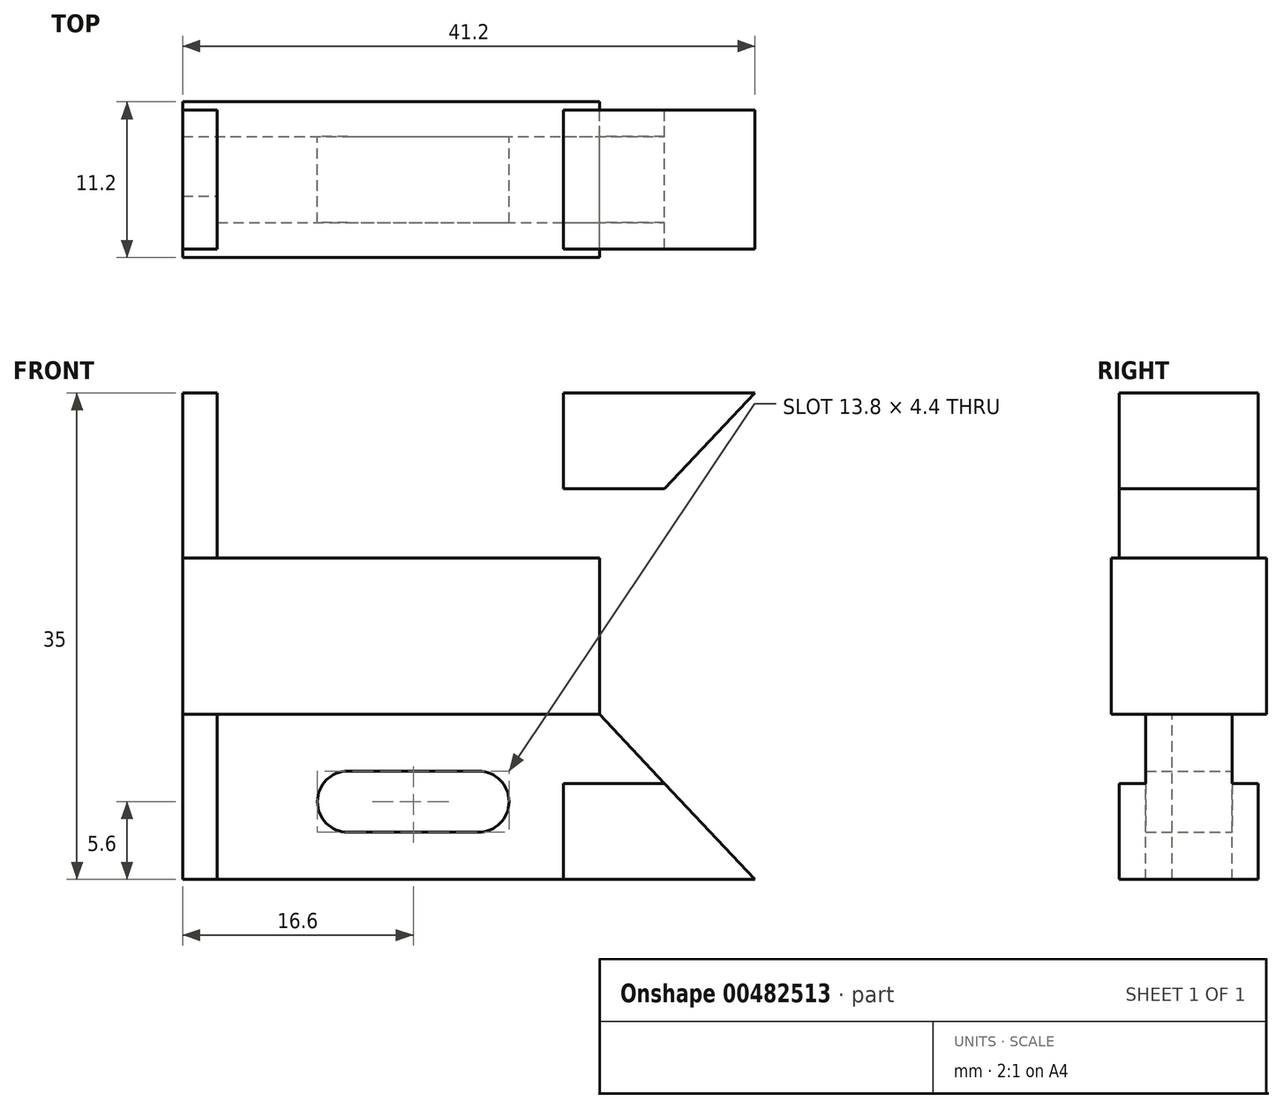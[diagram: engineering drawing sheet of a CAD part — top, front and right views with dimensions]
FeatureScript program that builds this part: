
annotation { "Feature Type Name" : "Feature", "Feature Type Description" : "" }
export const myFeature = defineFeature(function(context is Context, id is Id, definition is map)
    precondition{}
    {
        {
            var Q0;
            Q0=qCreatedBy(makeId("Front.planeOp"),FACE);
            var sketch = newSketch(context, id + "F0", { "sketchPlane" : qUnion([Q0])});
            skLineSegment(sketch, "E0.bottom", {"start": v(0, 0) * mm, "end": v(41.2, 0) * mm});
            skLineSegment(sketch, "E0.top", {"start": v(0, -11.88) * mm, "end": v(30, -11.88) * mm});
            skLineSegment(sketch, "E0.left", {"start": v(0, 0) * mm, "end": v(0, -11.88) * mm});
            skLineSegment(sketch, "E1.bottom", {"start": v(0, 0) * mm, "end": v(2.5, 0) * mm});
            skLineSegment(sketch, "E1.top", {"start": v(0, -11.88) * mm, "end": v(2.5, -11.88) * mm});
            skLineSegment(sketch, "E1.right", {"start": v(2.5, 0) * mm, "end": v(2.5, -11.88) * mm});
            skLineSegment(sketch, "E2.bottom", {"start": v(0, 0) * mm, "end": v(27.4, 0) * mm});
            skLineSegment(sketch, "E2.right", {"start": v(27.4, 0) * mm, "end": v(27.4, -6.9) * mm});
            skPoint(sketch, "E3.start.orphan", {"position": v(27.4, -6.9) * mm});
            skLineSegment(sketch, "E4", {"start": v(27.4, -6.9) * mm, "end": v(34.7, -6.9) * mm});
            skLineSegment(sketch, "E5", {"start": v(41.2, 0) * mm, "end": v(30, -11.88) * mm});
            skLineSegment(sketch, "E6.top", {"start": v(11.9, -3.4) * mm, "end": v(21.3, -3.4) * mm});
            skLineSegment(sketch, "E7.MirrorCS", {"start": v(11.9, -7.8) * mm, "end": v(21.3, -7.8) * mm});
            skLineSegment(sketch, "E8", {"start": v(23.5, -5.6) * mm, "end": v(23.5, -5.6) * mm});
            skLineSegment(sketch, "E9", {"start": v(9.7, -5.6) * mm, "end": v(9.7, -5.6) * mm});
            skPoint(sketch, "E10.visualSharp", {"position": v(9.7, -3.4) * mm});
            skArc(sketch, "E10.filletArc", {"start": v(11.9, -3.4) * mm, "mid": v(10.34, -4.04) * mm, "end": v(9.7, -5.6) * mm});
            skPoint(sketch, "E11.visualSharp", {"position": v(9.7, -7.8) * mm});
            skArc(sketch, "E11.filletArc", {"start": v(9.7, -5.6) * mm, "mid": v(10.34, -7.16) * mm, "end": v(11.9, -7.8) * mm});
            skPoint(sketch, "E12.visualSharp", {"position": v(23.5, -7.8) * mm});
            skArc(sketch, "E12.filletArc", {"start": v(21.3, -7.8) * mm, "mid": v(22.86, -7.16) * mm, "end": v(23.5, -5.6) * mm});
            skPoint(sketch, "E13.visualSharp", {"position": v(23.5, -3.4) * mm});
            skArc(sketch, "E13.filletArc", {"start": v(23.5, -5.6) * mm, "mid": v(22.86, -4.04) * mm, "end": v(21.3, -3.4) * mm});
            skLineSegment(sketch, "E14", {"start": v(0, -11.88) * mm, "end": v(0, -23.12) * mm});
            skLineSegment(sketch, "E15", {"start": v(0, -23.12) * mm, "end": v(30, -23.12) * mm});
            skLineSegment(sketch, "E16", {"start": v(30, -23.12) * mm, "end": v(30, -11.88) * mm});
            skLineSegment(sketch, "E17.MirrorCS", {"start": v(2.5, -35) * mm, "end": v(2.5, -23.13) * mm});
            skLineSegment(sketch, "E18.MirrorCS", {"start": v(0, -35) * mm, "end": v(0, -23.13) * mm});
            skLineSegment(sketch, "E19.MirrorCS", {"start": v(0, -35) * mm, "end": v(27.4, -35) * mm});
            skLineSegment(sketch, "E20.MirrorCS", {"start": v(0, -35) * mm, "end": v(41.2, -35) * mm});
            skLineSegment(sketch, "E21.MirrorCS", {"start": v(41.2, -35) * mm, "end": v(30, -23.12) * mm});
            skLineSegment(sketch, "E22.MirrorCS", {"start": v(27.4, -28.1) * mm, "end": v(34.7, -28.1) * mm});
            skLineSegment(sketch, "E23.MirrorCS", {"start": v(27.4, -35) * mm, "end": v(27.4, -28.1) * mm});
            skArc(sketch, "E24.MirrorCS", {"start": v(9.7, -29.4) * mm, "mid": v(10.34, -27.84) * mm, "end": v(11.9, -27.2) * mm});
            skArc(sketch, "E25.MirrorCS", {"start": v(11.9, -31.6) * mm, "mid": v(10.34, -30.96) * mm, "end": v(9.7, -29.4) * mm});
            skLineSegment(sketch, "E26.MirrorCS", {"start": v(11.9, -31.6) * mm, "end": v(21.3, -31.6) * mm});
            skLineSegment(sketch, "E27.MirrorCS", {"start": v(11.9, -27.2) * mm, "end": v(21.3, -27.2) * mm});
            skArc(sketch, "E28.MirrorCS", {"start": v(21.3, -27.2) * mm, "mid": v(22.86, -27.84) * mm, "end": v(23.5, -29.4) * mm});
            skArc(sketch, "E29.MirrorCS", {"start": v(23.5, -29.4) * mm, "mid": v(22.86, -30.96) * mm, "end": v(21.3, -31.6) * mm});
            skPoint(sketch, "E30.end.orphan", {"position": v(30, -17.5) * mm});
            skPoint(sketch, "E30.start.orphan", {"position": v(0, -17.5) * mm});
            skSolve(sketch);
        }
        {
            var Q0;
            Q0=makeQuery(id+"F0.imprint","IMPRINT",FACE,{"disambiguationData":[TD([[makeQuery(id+"F0.imprint","IMPRINT",EDGE,{"derivedFrom":sQuery(id+"F0.wireOp",EDGE,"E0.top")}),-1.0]])]});
            extrude(context, id + "F1", {"entities" : qUnion([Q0]), "depth" : 5.6 * mm, "hasSecondDirection" : true, "secondDirectionOppositeDirection" : true, "secondDirectionDepth" : 5.6 * mm});
        }
        {
            var Q0;
            {var subQ1=sQuery(id+"F0.wireOp",EDGE,"E0.top");Q0=makeQuery(id+"F0.imprint","IMPRINT",FACE,{"disambiguationData":[TD([[makeQuery(id+"F0.imprint","IMPRINT",EDGE,{"derivedFrom":subQ1}),1.0]])]});}
            var Q1;
            {var subQ5=sQuery(id+"F0.wireOp",EDGE,"E17.MirrorCS");Q1=makeQuery(id+"F0.imprint","IMPRINT",FACE,{"disambiguationData":[TD([[makeQuery(id+"F0.imprint","IMPRINT",EDGE,{"derivedFrom":subQ5}),-1.0]])]});}
            extrude(context, id + "F2", {"entities" : qUnion([Q0, Q1]), "operationType" : NewBodyOperationType.ADD, "depth" : 3.1 * mm, "hasSecondDirection" : true, "secondDirectionOppositeDirection" : true, "secondDirectionDepth" : 3.1 * mm});
        }
        {
            var Q0;
            Q0=makeQuery(id+"F0.imprint","IMPRINT",FACE,{"disambiguationData":[TD([[makeQuery(id+"F0.imprint","IMPRINT",EDGE,{"derivedFrom":sQuery(id+"F0.wireOp",EDGE,"E1.top")}),1.0]])]});
            var Q1;
            {var subQ2=sQuery(id+"F0.wireOp",EDGE,"E17.MirrorCS");Q1=makeQuery(id+"F0.imprint","IMPRINT",FACE,{"disambiguationData":[TD([[makeQuery(id+"F0.imprint","IMPRINT",EDGE,{"derivedFrom":subQ2}),1.0]])]});}
            extrude(context, id + "F3", {"entities" : qUnion([Q0, Q1]), "operationType" : NewBodyOperationType.ADD, "depth" : 1.2 * mm, "hasSecondDirection" : true, "secondDirectionOppositeDirection" : true, "secondDirectionDepth" : 3.1 * mm});
        }
        {
            var Q0;
            {var subQ0=sQuery(id+"F0.wireOp",EDGE,"E0.bottom");Q0=makeQuery(id+"F0.imprint","IMPRINT",FACE,{"disambiguationData":[TD([[makeQuery(id+"F0.imprint","IMPRINT",EDGE,{"derivedFrom":subQ0}),-1.0]])]});}
            var Q1;
            {var subQ4=sQuery(id+"F0.wireOp",EDGE,"E22.MirrorCS");Q1=makeQuery(id+"F0.imprint","IMPRINT",FACE,{"disambiguationData":[TD([[makeQuery(id+"F0.imprint","IMPRINT",EDGE,{"derivedFrom":subQ4}),-1.0]])]});}
            extrude(context, id + "F4", {"entities" : qUnion([Q0, Q1]), "operationType" : NewBodyOperationType.ADD, "depth" : 5 * mm, "hasSecondDirection" : true, "secondDirectionOppositeDirection" : true, "secondDirectionDepth" : 5 * mm});
        }
    });
